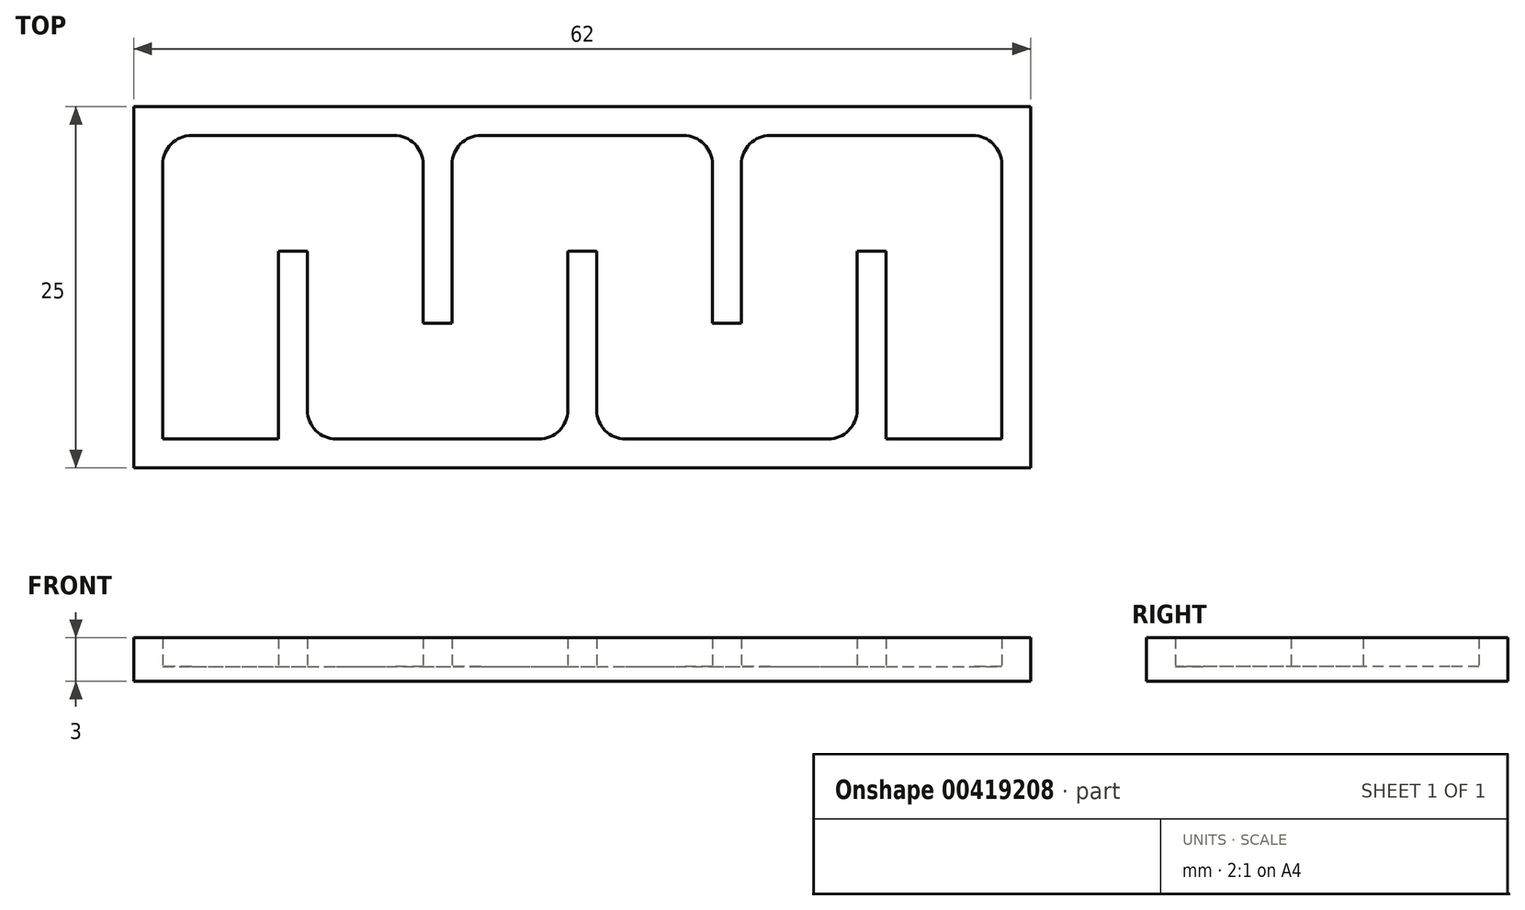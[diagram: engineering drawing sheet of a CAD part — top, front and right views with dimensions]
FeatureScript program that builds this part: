
annotation { "Feature Type Name" : "Feature", "Feature Type Description" : "" }
export const myFeature = defineFeature(function(context is Context, id is Id, definition is map)
    precondition{}
    {
        {
            var Q0;
            Q0=qCreatedBy(makeId("Top.planeOp"),FACE);
            var sketch = newSketch(context, id + "F0", { "sketchPlane" : qUnion([Q0])});
            skLineSegment(sketch, "E0.bottom", {"start": v(31, 12.5) * mm, "end": v(-31, 12.5) * mm});
            skLineSegment(sketch, "E0.top", {"start": v(31, -12.5) * mm, "end": v(-31, -12.5) * mm});
            skLineSegment(sketch, "E0.left", {"start": v(31, 12.5) * mm, "end": v(31, -12.5) * mm});
            skLineSegment(sketch, "E0.right", {"start": v(-31, 12.5) * mm, "end": v(-31, -12.5) * mm});
            skPoint(sketch, "E0.middle", {"position": v(0, 0) * mm});
            skSolve(sketch);
        }
        {
            var Q0;
            Q0=makeQuery(id+"F0.imprint","IMPRINT",FACE,{"disambiguationData":[TD([[makeQuery(id+"F0.imprint","IMPRINT",EDGE,{"derivedFrom":sQuery(id+"F0.wireOp",EDGE,"E0.bottom")}),1.0]])]});
            extrude(context, id + "F1", {"entities" : qUnion([Q0]), "depth" : 1 * mm});
        }
        {
            var Q0;
            Q0=makeQuery(id+"F1.opExtrude","CAP_FACE",FACE,{"disambiguationData":[OSD([sQuery(id+"F0.wireOp",EDGE,"E0.bottom"),sQuery(id+"F0.wireOp",EDGE,"E0.top"),sQuery(id+"F0.wireOp",EDGE,"E0.left"),sQuery(id+"F0.wireOp",EDGE,"E0.right")])],"isStart":false});
            var sketch = newSketch(context, id + "F2", { "sketchPlane" : qUnion([Q0])});
            skLineSegment(sketch, "E1.bottom", {"start": v(-31, 12.5) * mm, "end": v(31, 12.5) * mm});
            skLineSegment(sketch, "E1.top", {"start": v(-31, -12.5) * mm, "end": v(31, -12.5) * mm});
            skLineSegment(sketch, "E1.left", {"start": v(-31, 12.5) * mm, "end": v(-31, -12.5) * mm});
            skLineSegment(sketch, "E1.right", {"start": v(31, 12.5) * mm, "end": v(31, -12.5) * mm});
            skLineSegment(sketch, "E2.bottom", {"start": v(-27, 10.5) * mm, "end": v(-13, 10.5) * mm});
            skLineSegment(sketch, "E2.top", {"start": v(-29, -10.5) * mm, "end": v(-21, -10.5) * mm});
            skLineSegment(sketch, "E2.left", {"start": v(-29, 8.5) * mm, "end": v(-29, -10.5) * mm});
            skLineSegment(sketch, "E2.right", {"start": v(29, 8.5) * mm, "end": v(29, -10.5) * mm});
            skLineSegment(sketch, "E3.bottom", {"start": v(-21, 2.5) * mm, "end": v(-19, 2.5) * mm});
            skLineSegment(sketch, "E3.left", {"start": v(-21, 2.5) * mm, "end": v(-21, -10.5) * mm});
            skLineSegment(sketch, "E3.right", {"start": v(-19, 2.5) * mm, "end": v(-19, -8.5) * mm});
            skLineSegment(sketch, "E4.top", {"start": v(-11, -2.5) * mm, "end": v(-9, -2.5) * mm});
            skLineSegment(sketch, "E4.left", {"start": v(-11, 8.5) * mm, "end": v(-11, -2.5) * mm});
            skLineSegment(sketch, "E4.right", {"start": v(-9, 8.5) * mm, "end": v(-9, -2.5) * mm});
            skLineSegment(sketch, "E5.bottom", {"start": v(-1, 2.5) * mm, "end": v(1, 2.5) * mm});
            skLineSegment(sketch, "E5.left", {"start": v(-1, 2.5) * mm, "end": v(-1, -8.5) * mm});
            skLineSegment(sketch, "E5.right", {"start": v(1, 2.5) * mm, "end": v(1, -8.5) * mm});
            skLineSegment(sketch, "E6.top", {"start": v(9, -2.5) * mm, "end": v(11, -2.5) * mm});
            skLineSegment(sketch, "E6.left", {"start": v(9, 8.5) * mm, "end": v(9, -2.5) * mm});
            skLineSegment(sketch, "E6.right", {"start": v(11, 8.5) * mm, "end": v(11, -2.5) * mm});
            skLineSegment(sketch, "E7.bottom", {"start": v(19, 2.5) * mm, "end": v(21, 2.5) * mm});
            skLineSegment(sketch, "E7.left", {"start": v(19, 2.5) * mm, "end": v(19, -8.5) * mm});
            skLineSegment(sketch, "E7.right", {"start": v(21, 2.5) * mm, "end": v(21, -10.5) * mm});
            skLineSegment(sketch, "E8.trimOffspring", {"start": v(-7, 10.5) * mm, "end": v(7, 10.5) * mm});
            skLineSegment(sketch, "E9.trimOffspring", {"start": v(13, 10.5) * mm, "end": v(27, 10.5) * mm});
            skLineSegment(sketch, "E10.trimOffspring", {"start": v(-17, -10.5) * mm, "end": v(-3, -10.5) * mm});
            skLineSegment(sketch, "E11.trimOffspring", {"start": v(3, -10.5) * mm, "end": v(17, -10.5) * mm});
            skLineSegment(sketch, "E12.trimOffspring", {"start": v(21, -10.5) * mm, "end": v(29, -10.5) * mm});
            skPoint(sketch, "E13.visualSharp", {"position": v(-29, 10.5) * mm});
            skArc(sketch, "E13.filletArc", {"start": v(-27, 10.5) * mm, "mid": v(-28.41, 9.91) * mm, "end": v(-29, 8.5) * mm});
            skPoint(sketch, "E14.visualSharp", {"position": v(-11, 10.5) * mm});
            skArc(sketch, "E14.filletArc", {"start": v(-11, 8.5) * mm, "mid": v(-11.59, 9.91) * mm, "end": v(-13, 10.5) * mm});
            skPoint(sketch, "E15.visualSharp", {"position": v(-9, 10.5) * mm});
            skArc(sketch, "E15.filletArc", {"start": v(-7, 10.5) * mm, "mid": v(-8.41, 9.91) * mm, "end": v(-9, 8.5) * mm});
            skPoint(sketch, "E16.visualSharp", {"position": v(9, 10.5) * mm});
            skArc(sketch, "E16.filletArc", {"start": v(9, 8.5) * mm, "mid": v(8.41, 9.91) * mm, "end": v(7, 10.5) * mm});
            skPoint(sketch, "E17.visualSharp", {"position": v(11, 10.5) * mm});
            skArc(sketch, "E17.filletArc", {"start": v(13, 10.5) * mm, "mid": v(11.59, 9.91) * mm, "end": v(11, 8.5) * mm});
            skPoint(sketch, "E18.visualSharp", {"position": v(1, -10.5) * mm});
            skArc(sketch, "E18.filletArc", {"start": v(1, -8.5) * mm, "mid": v(1.59, -9.91) * mm, "end": v(3, -10.5) * mm});
            skPoint(sketch, "E19.visualSharp", {"position": v(-19, -10.5) * mm});
            skArc(sketch, "E19.filletArc", {"start": v(-19, -8.5) * mm, "mid": v(-18.41, -9.91) * mm, "end": v(-17, -10.5) * mm});
            skPoint(sketch, "E20.visualSharp", {"position": v(-1, -10.5) * mm});
            skArc(sketch, "E20.filletArc", {"start": v(-3, -10.5) * mm, "mid": v(-1.59, -9.91) * mm, "end": v(-1, -8.5) * mm});
            skPoint(sketch, "E21.visualSharp", {"position": v(19, -10.5) * mm});
            skArc(sketch, "E21.filletArc", {"start": v(17, -10.5) * mm, "mid": v(18.41, -9.91) * mm, "end": v(19, -8.5) * mm});
            skPoint(sketch, "E22.visualSharp", {"position": v(29, 10.5) * mm});
            skArc(sketch, "E22.filletArc", {"start": v(29, 8.5) * mm, "mid": v(28.41, 9.91) * mm, "end": v(27, 10.5) * mm});
            skSolve(sketch);
        }
        {
            var Q0;
            Q0 = qSketchRegion(id + "F2", true);
            var Q1;
            Q1=makeQuery(id+"F2.imprint","IMPRINT",FACE,{"disambiguationData":[TD([[makeQuery(id+"F2.imprint","IMPRINT",EDGE,{"derivedFrom":sQuery(id+"F2.wireOp",EDGE,"E3.bottom")}),-1.0]])]});
            var Q2;
            Q2=makeQuery(id+"F2.imprint","IMPRINT",FACE,{"disambiguationData":[TD([[makeQuery(id+"F2.imprint","IMPRINT",EDGE,{"derivedFrom":sQuery(id+"F2.wireOp",EDGE,"E4.bottom")}),-1.0]])]});
            var Q3;
            Q3=makeQuery(id+"F2.imprint","IMPRINT",FACE,{"disambiguationData":[TD([[makeQuery(id+"F2.imprint","IMPRINT",EDGE,{"derivedFrom":sQuery(id+"F2.wireOp",EDGE,"E5.bottom")}),-1.0]])]});
            var Q4;
            Q4=makeQuery(id+"F2.imprint","IMPRINT",FACE,{"disambiguationData":[TD([[makeQuery(id+"F2.imprint","IMPRINT",EDGE,{"derivedFrom":sQuery(id+"F2.wireOp",EDGE,"E6.bottom")}),-1.0]])]});
            var Q5;
            Q5=makeQuery(id+"F2.imprint","IMPRINT",FACE,{"disambiguationData":[TD([[makeQuery(id+"F2.imprint","IMPRINT",EDGE,{"derivedFrom":sQuery(id+"F2.wireOp",EDGE,"E7.bottom")}),-1.0]])]});
            extrude(context, id + "F3", {"entities" : qUnion([Q0, Q1, Q2, Q3, Q4, Q5]), "operationType" : NewBodyOperationType.ADD, "depth" : 2 * mm});
        }
    });
